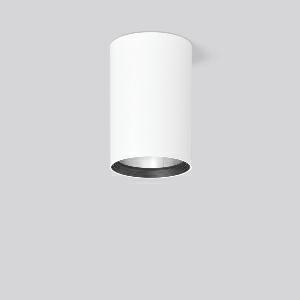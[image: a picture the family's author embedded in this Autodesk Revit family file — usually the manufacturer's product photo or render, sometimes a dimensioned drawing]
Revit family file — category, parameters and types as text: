
# Revit family: heledon_maxi_a_931226_002_3_76_057d
name_source: partatom
category: Lighting Fixtures
units: mm (PartAtom-declared; Revit-internal decimal feet)

## family parameters
Cut with Voids When Loaded = No
Host = Face
Light Source = No
Part Type = Normal
Room Calculation Point = No
Round Connector Dimension = Use Diameter
Shared = No

## types (1)
- HELEDON maxi A (1 x LED Modul 935, 4200 lm, 3500)
    Apparent Load = 35 VA
    Approval mark = CE
    CIE Flux Codes = 97 100 100 100 100
    Color Rendering = 92
    Color Temperature = 3500
    Default Elevation = 1800 mm
    Description = Series: HELEDON maxi
Cylindrical surface-mounted downlight. Housing: die-cast aluminium, powder-coated. Internal ceiling frame polycarbonate with bayonet mounting. Black plastic ring and recessed LED to prevent glare from the side. Optical assembly with reflector made of MIRO-Silver with 98% total light reflection for outstanding efficiency - can be changed without tools. Best colour rendering index Ra>90. Suitable for Ceiling mounting. Easy installation with a separate ceiling frame with bayonet mounting and plug connection. Driver integrated. Connected via plug-in connector. High quality converter without flickering and stroboscopic effect. The following accessories can be mounted without use of tools: interchangeable lenses, decorative glasses, honeycomb louvre, clear and frosted diffusers, white interchangeable plastic ring. 
Colour: traffic white, matt (RAL 9016)
Diameter: 123 mm
Height: 183 mm
Lamp: LED
Socket: without socket
Colour temperature: 3500K
Colour rendering index (CRI): 92
System power: 35 W
Rated luminous flux: 4200 lm
Luminous efficiency: 120 lm/W
Control gear: Converter, dimmable, DALI
Protection class: I
Type of protection: IP 20
    Height = 183 mm
    Lamp = 1 x LED Modul 935
    Lamp Light Flux = 4200 lm
    Lamp count = 1
    Length = 123 mm
    Lifetime = 50000 h
    Luminous efficacy = 120 lm/W
    Manufacturer = RZB
    ModVariant = No
    Model = 931226.002.3.76
    Mounting Place = Ceiling
    Mounting Type = Surface mounted
    Number of Poles = 1
    OnlyDefault = Yes
    Power Factor = 1
    Product Name = HELEDON maxi A
    Product group = Surface mounted downlights
    ProductGroupID = 302
    Protection Class = Protection class I
    Protection Degree = IP 20
    RLX_Detail_Level = 1
    RLX_Emergency_Light_Flux = 0 lm
    RLX_Emergency_Type = 0
    RLX_Emergency_Type_DB = No
    RlxData = <blob elided: 98045 chars, md5=d74f1de8>
    Socket = socket
    Standby Power = 0 W
    System Light Flux = 4200 lm
    System Power = 35 W
    Type Comments = Product without accessories
    Type Image = 931192.002.jpg
    URL = http://relux.com
    VarID = ---
    Voltage = 230 V
    Voltage Range = 220-240 V
    Weight = 0.00 kg
    Width = 0 mm  [stored 0 ft]

note: [stored X ft] marks values corroborated as IEEE doubles in the binary element streams (Revit-internal decimal feet)

## geometry (parser evidence)
native form markers: Blend x4, Sweep x10
no freeform markers — native parametric forms only
